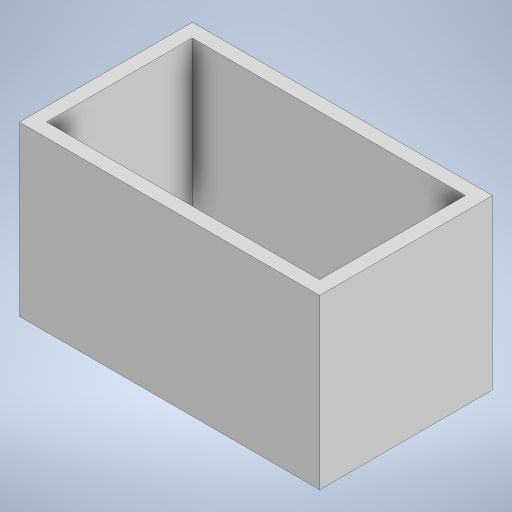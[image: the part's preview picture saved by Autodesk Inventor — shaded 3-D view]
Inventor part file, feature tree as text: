
AUTODESK INVENTOR PART (.ipt)
format: ipt  version: 2023 (Build 270158000, 158)  size: 240,128 bytes
history: native  units: mm
features: extrude x6, sketch x5, other x1
ambient origin geometry x8: Origin, YZ Plane, XZ Plane, XY Plane, X Axis, Y Axis, Z Axis, Center Point
bodies: Body1 (feature_tree)
feature tree (12):
  other  "솔리드1"
  sketch  "스케치1"
  extrude  "돌출1"  Depth=60.0mm
  extrude  "돌출2"  Depth=32.0mm
  extrude  "돌출3"  Depth=3.0mm
  extrude  "돌출4"  Depth=3.0mm TaperAngle=0.0deg
  extrude  "돌출5"  Depth=34.0mm TaperAngle=0.0deg
  extrude  "돌출6"  Depth=2.0mm
  sketch  "스케치2"
  sketch  "스케치3"
  sketch  "스케치4"
  sketch  "스케치5"
